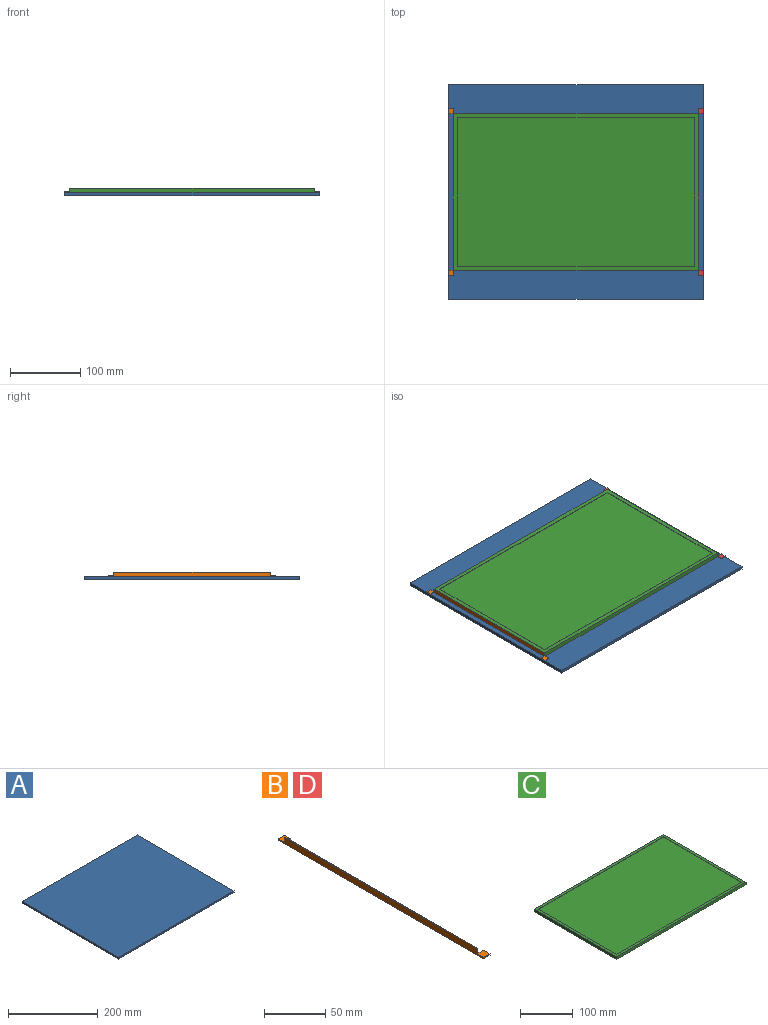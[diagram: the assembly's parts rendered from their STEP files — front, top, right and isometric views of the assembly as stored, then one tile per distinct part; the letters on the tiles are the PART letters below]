
ASSEMBLY  parts=4 mates=3
PART A: 6 faces, bbox 362x304.8x4.5 mm
  f0: plane 304.8x4.52mm, normal (1,0,0), area 1378.1mm2, adj f1,f3,f4,f5
  f1: plane 361.95x4.52mm, normal (0,1,0), area 1636.4mm2, adj f0,f2,f4,f5
  f2: plane 304.8x4.52mm, normal (-1,0,0), area 1378.1mm2, adj f1,f3,f4,f5
  f3: plane 361.95x4.52mm, normal (0,-1,0), area 1636.4mm2, adj f0,f2,f4,f5
  f4: plane 361.95x304.8mm, normal (0,0,1), area 110322.4mm2, adj f0,f1,f2,f3
  f5: plane 361.95x304.8mm, normal (0,0,-1), area 110322.4mm2, adj f0,f1,f2,f3
PART B: 14 faces, bbox 7.4x236.8x6.4 mm
  f0: plane 236.77x6.35mm, normal (-1,0,0), area 1428.1mm2, adj f1,f3,f4,f5,f7,f9,f12,f13
  f1: plane 5.08x0.64mm, normal (0,-1,0), area 3.3mm2, adj f0,f2,f4,f9
  f2: plane 221.93x6.35mm, normal (1,0,0), area 1409.3mm2, adj f1,f3,f4,f5,f6,f10
  f3: plane 5.08x0.64mm, normal (0,1,0), area 3.3mm2, adj f0,f2,f4,f13
  f4: plane 221.93x0.64mm, normal (0,0,1), area 142.4mm2, adj f0,f1,f2,f3
  f5: plane 236.77x7.42mm, normal (0,0,-1), area 252.4mm2, adj f0,f2,f6,f7,f8,f10,f11,f12
  f6: plane 6.78x1.27mm, normal (0,1,0), area 8.6mm2, adj f2,f5,f8,f9
  f7: plane 7.42x1.27mm, normal (0,-1,0), area 9.4mm2, adj f0,f5,f8,f9
  f8: plane 7.42x1.27mm, normal (1,0,0), area 9.4mm2, adj f5,f6,f7,f9
  f9: plane 7.42x7.42mm, normal (0,0,1), area 55mm2, adj f0,f1,f6,f7,f8
  f10: plane 6.78x1.27mm, normal (0,-1,0), area 8.6mm2, adj f2,f5,f11,f13
  f11: plane 7.42x1.27mm, normal (1,0,0), area 9.4mm2, adj f5,f10,f12,f13
  f12: plane 7.42x1.27mm, normal (0,1,0), area 9.4mm2, adj f0,f5,f11,f13
  f13: plane 7.42x7.42mm, normal (0,0,1), area 55mm2, adj f0,f3,f10,f11,f12
PART C: 11 faces, bbox 347.1x221.9x6.4 mm
  f0: plane 347.14x6.35mm, normal (0,1,0), area 2204.3mm2, adj f1,f7,f8,f9
  f1: plane 221.93x6.35mm, normal (-1,0,0), area 1409.3mm2, adj f0,f2,f8,f9
  f2: plane 347.14x6.35mm, normal (0,-1,0), area 2204.3mm2, adj f1,f7,f8,f9
  f3: plane 210.82x0.57mm, normal (1,0,0), area 120.5mm2, adj f4,f6,f8,f10
  f4: plane 336.03x0.57mm, normal (0,-1,0), area 192mm2, adj f3,f5,f8,f10
  f5: plane 210.82x0.57mm, normal (-1,0,0), area 120.5mm2, adj f4,f6,f8,f10
  f6: plane 336.03x0.57mm, normal (0,1,0), area 192mm2, adj f3,f5,f8,f10
  f7: plane 221.93x6.35mm, normal (1,0,0), area 1409.3mm2, adj f0,f2,f8,f9
  f8: plane 347.14x221.93mm, normal (0,0,1), area 6200.3mm2, adj f0,f1,f2,f3,f4,f5,f6,f7
  f9: plane 347.14x221.93mm, normal (0,0,-1), area 77041.8mm2, adj f0,f1,f2,f7
  f10: plane 336.03x210.82mm, normal (0,0,1), area 70841.5mm2, adj f3,f4,f5,f6
PART D: same geometry as B
PLACE A t=(567.64,-130.1,-88.77)mm
PLACE B rot(axis=(0,0,1),180deg) t=(57.36,-12.2,-84.21)mm
PLACE C t=(1034.75,-159.45,-84.25)mm
PLACE D t=(1034.57,-159.45,-84.21)mm
MATE fastened D.f0 <-> C.f7  axis (-1,0,0) through (719.53,-85.82,-81.07)mm
MATE fastened A.f4 <-> C.f9  axis (0,0,1) through (545.96,-85.82,-84.25)mm
MATE fastened B.f0 <-> C.f1  axis (1,0,0) through (372.39,-85.82,-81.07)mm
